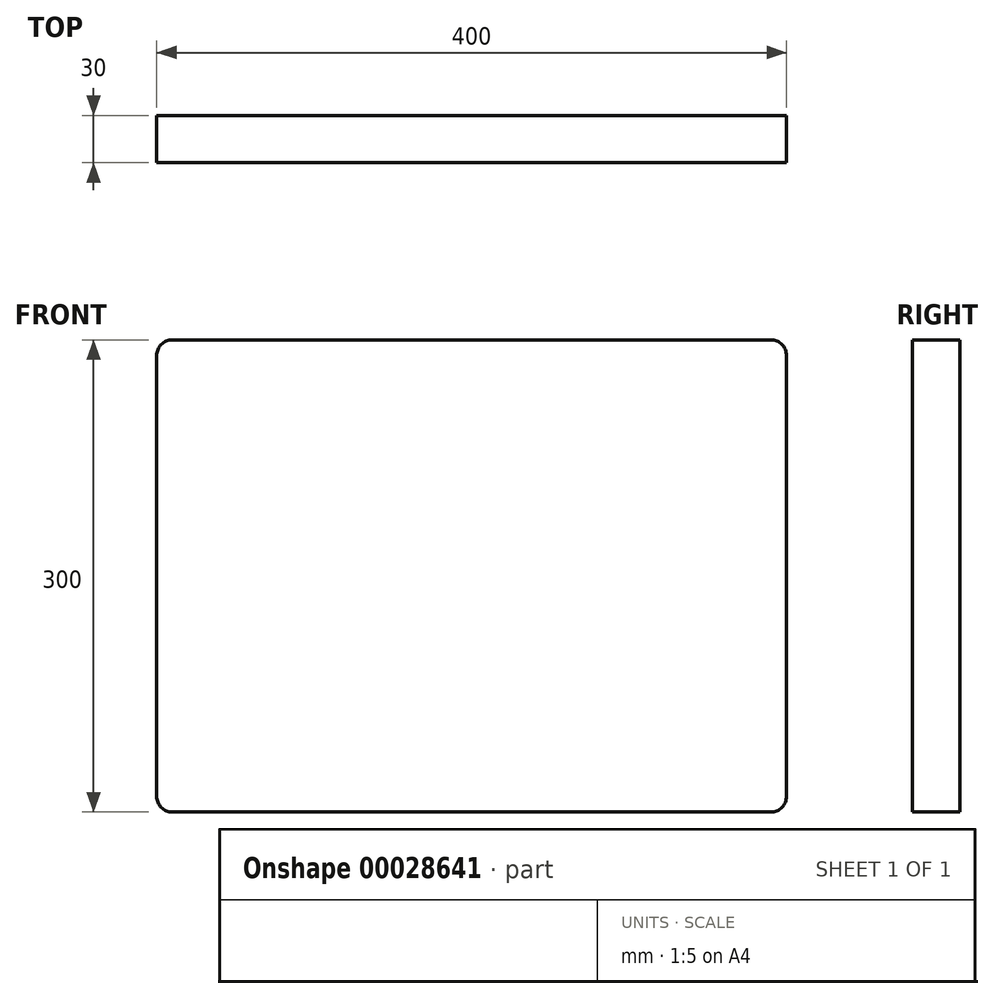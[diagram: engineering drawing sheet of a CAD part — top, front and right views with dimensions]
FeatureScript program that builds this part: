
annotation { "Feature Type Name" : "Feature", "Feature Type Description" : "" }
export const myFeature = defineFeature(function(context is Context, id is Id, definition is map)
    precondition{}
    {
        {
            var Q0;
            Q0=qCreatedBy(makeId("Front.planeOp"),FACE);
            var sketch = newSketch(context, id + "F0", { "sketchPlane" : qUnion([Q0])});
            skLineSegment(sketch, "E0.rect.bottom", {"start": v(200, -150) * mm, "end": v(-200, -150) * mm});
            skLineSegment(sketch, "E0.rect.top", {"start": v(200, 150) * mm, "end": v(-200, 150) * mm});
            skLineSegment(sketch, "E0.rect.left", {"start": v(200, -150) * mm, "end": v(200, 150) * mm});
            skLineSegment(sketch, "E0.rect.right", {"start": v(-200, -150) * mm, "end": v(-200, 150) * mm});
            skPoint(sketch, "E0.rect.middle", {"position": v(0, 0) * mm});
            skSolve(sketch);
        }
        {
            var Q0;
            Q0=makeQuery(id+"F0.imprint","IMPRINT",FACE,{"disambiguationData":[TD([[makeQuery(id+"F0.imprint","IMPRINT",EDGE,{"derivedFrom":sQuery(id+"F0.wireOp",EDGE,"E0.rect.bottom")}),-1.0]])]});
            extrude(context, id + "F1", {"entities" : qUnion([Q0]), "flatOperationType" : FlatOperationType.REMOVE, "offsetDistance" : 25 * mm, "depth" : 30 * mm, "domain" : OperationDomain.MODEL, "symmetric" : true});
        }
        {
            var Q0;
            Q0=makeQuery(id+"F1.opExtrude","SWEPT_EDGE",EDGE,{"disambiguationData":[OSD([sQuery(id+"F0.wireOp",EDGE,"E0.rect.bottom"),sQuery(id+"F0.wireOp",EDGE,"E0.rect.right")])]});
            var Q1;
            Q1=makeQuery(id+"F1.opExtrude","SWEPT_EDGE",EDGE,{"disambiguationData":[OSD([sQuery(id+"F0.wireOp",EDGE,"E0.rect.top"),sQuery(id+"F0.wireOp",EDGE,"E0.rect.right")])]});
            var Q2;
            Q2=makeQuery(id+"F1.opExtrude","SWEPT_EDGE",EDGE,{"disambiguationData":[OSD([sQuery(id+"F0.wireOp",EDGE,"E0.rect.top"),sQuery(id+"F0.wireOp",EDGE,"E0.rect.left")])]});
            var Q3;
            Q3=makeQuery(id+"F1.opExtrude","SWEPT_EDGE",EDGE,{"disambiguationData":[OSD([sQuery(id+"F0.wireOp",EDGE,"E0.rect.bottom"),sQuery(id+"F0.wireOp",EDGE,"E0.rect.left")])]});
            fillet(context, id + "F2", {"entities" : qUnion([Q0, Q1, Q2, Q3]), "radius" : 10 * mm, "tangentPropagation" : true, "allowEdgeOverflow" : false});
        }
    });
